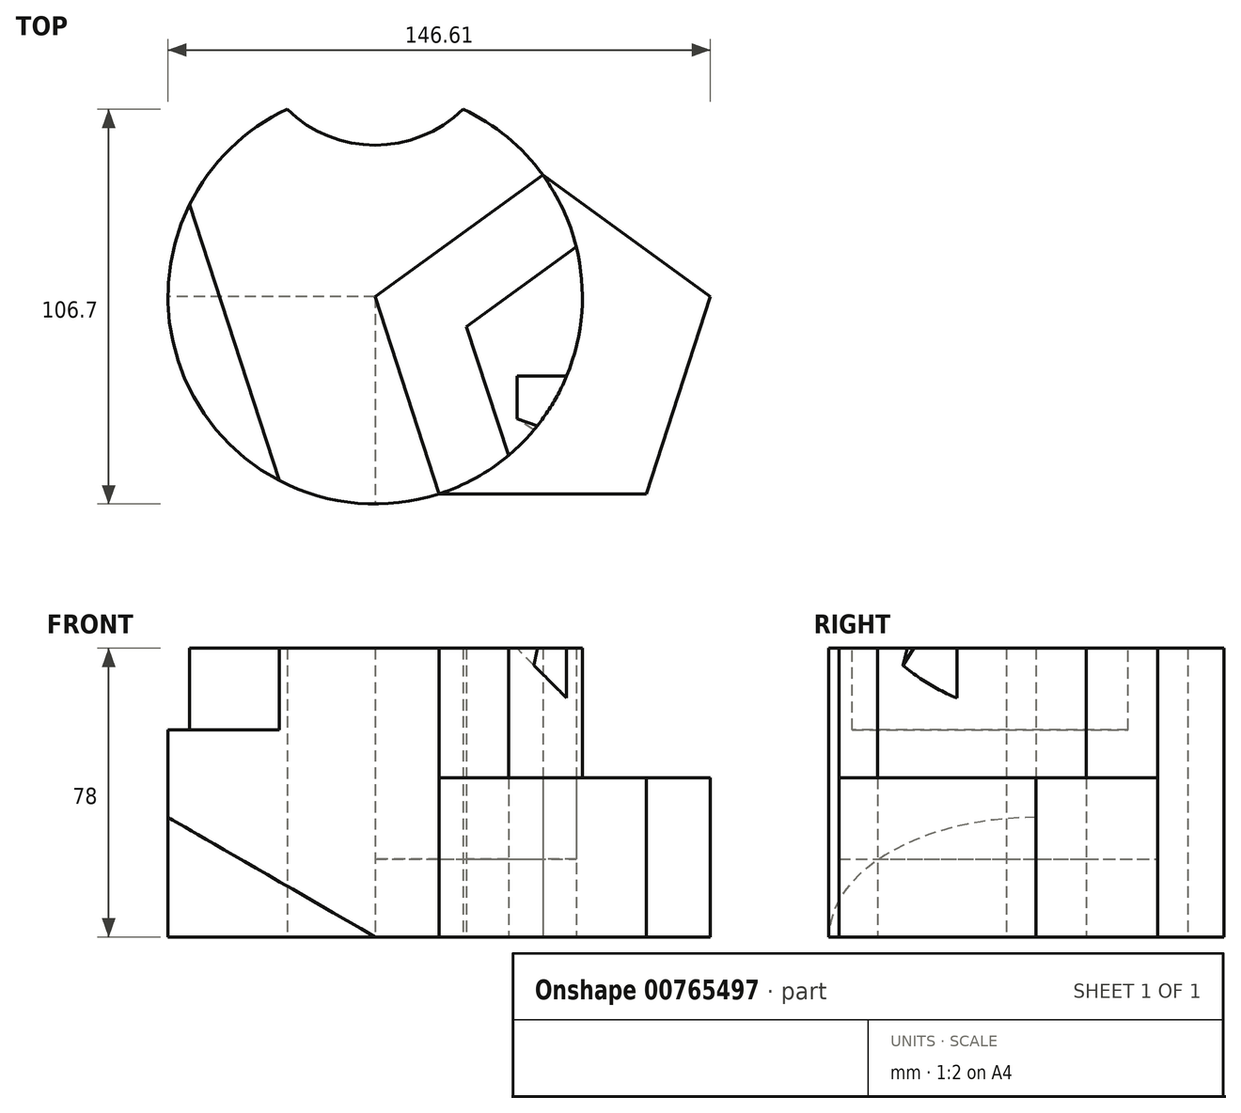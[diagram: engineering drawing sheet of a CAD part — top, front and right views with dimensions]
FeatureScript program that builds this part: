
annotation { "Feature Type Name" : "Feature", "Feature Type Description" : "" }
export const myFeature = defineFeature(function(context is Context, id is Id, definition is map)
    precondition{}
    {
        {
            var Q0;
            Q0=qCreatedBy(makeId("Top.planeOp"),FACE);
            var sketch = newSketch(context, id + "F0", { "sketchPlane" : qUnion([Q0])});
            skCircle(sketch, "E0.cCircle", {"center": v(45.3, -14.72) * mm, "radius": 47.64 * mm, "construction": true});
            skLineSegment(sketch, "E0.0", {"start": v(0, 0) * mm, "end": v(45.3, 32.92) * mm});
            skLineSegment(sketch, "E0.1", {"start": v(45.3, 32.92) * mm, "end": v(90.6, 0) * mm});
            skLineSegment(sketch, "E0.2", {"start": v(90.6, 0) * mm, "end": v(73.3, -53.26) * mm});
            skLineSegment(sketch, "E0.3", {"start": v(73.3, -53.26) * mm, "end": v(17.3, -53.26) * mm});
            skLineSegment(sketch, "E0.4", {"start": v(17.3, -53.26) * mm, "end": v(0, 0) * mm});
            skLineSegment(sketch, "E1", {"start": v(0, 0) * mm, "end": v(56, 0) * mm, "construction": true});
            skLineSegment(sketch, "E2", {"start": v(0, 0) * mm, "end": v(0, 75) * mm, "construction": true});
            skArc(sketch, "E3", {"start": v(-23.78, 50.7) * mm, "mid": v(0, -56) * mm, "end": v(23.78, 50.7) * mm});
            skArc(sketch, "E4", {"start": v(-23.78, 50.7) * mm, "mid": v(0, 41) * mm, "end": v(23.78, 50.7) * mm});
            skLineSegment(sketch, "E5", {"start": v(45.3, -14.72) * mm, "end": v(0, 0) * mm, "construction": true});
            skLineSegment(sketch, "E6", {"start": v(36.01, -42.88) * mm, "end": v(24.69, -8.02) * mm});
            skLineSegment(sketch, "E7", {"start": v(24.69, -8.02) * mm, "end": v(54.34, 13.52) * mm});
            skSolve(sketch);
        }
        {
            var Q0;
            {var subQ1=sQuery(id+"F0.wireOp",EDGE,"E0.0");Q0=makeQuery(id+"F0.imprint","IMPRINT",FACE,{"disambiguationData":[TD([[makeQuery(id+"F0.imprint","IMPRINT",EDGE,{"derivedFrom":subQ1}),1.0]])]});}
            var Q1;
            {var subQ0=sQuery(id+"F0.wireOp",EDGE,"E6");Q1=makeQuery(id+"F0.imprint","IMPRINT",FACE,{"disambiguationData":[TD([[makeQuery(id+"F0.imprint","IMPRINT",EDGE,{"derivedFrom":subQ0}),-1.0]])]});}
            extrude(context, id + "F1", {"entities" : qUnion([Q0, Q1]), "depth" : 78 * mm, "offsetDistance" : 25 * mm});
        }
        {
            var Q0;
            {var subQ3=sQuery(id+"F0.wireOp",EDGE,"E0.1");Q0=makeQuery(id+"F0.imprint","IMPRINT",FACE,{"disambiguationData":[TD([[makeQuery(id+"F0.imprint","IMPRINT",EDGE,{"derivedFrom":subQ3}),-1.0]])]});}
            extrude(context, id + "F2", {"entities" : qUnion([Q0]), "operationType" : NewBodyOperationType.ADD, "depth" : 43 * mm, "offsetDistance" : 25 * mm});
        }
        {
            var Q0;
            Q0=makeQuery(id+"F1.opExtrude","CAP_FACE",FACE,{"disambiguationData":[OSD([sQuery(id+"F0.wireOp",EDGE,"E3"),sQuery(id+"F0.wireOp",EDGE,"E4")])],"isStart":false});
            var sketch = newSketch(context, id + "F3", { "sketchPlane" : qUnion([Q0])});
            skLineSegment(sketch, "E8", {"start": v(-25.93, -49.63) * mm, "end": v(-50.15, 24.91) * mm});
            skSolve(sketch);
        }
        {
            var Q0;
            {var subQ0=sQuery(id+"F3.wireOp",EDGE,"E8");Q0=makeQuery(id+"F3.imprint","IMPRINT",FACE,{"disambiguationData":[TD([[makeQuery(id+"F3.imprint","IMPRINT",EDGE,{"derivedFrom":subQ0}),1.0]])]});}
            extrude(context, id + "F4", {"entities" : qUnion([Q0]), "operationType" : NewBodyOperationType.REMOVE, "oppositeDirection" : true, "depth" : 22 * mm, "offsetDistance" : 25 * mm});
        }
        {
            var Q0;
            Q0=qCreatedBy(makeId("Front.planeOp"),FACE);
            cPlane(context, id + "F5", {"entities" : qUnion([Q0]), "cplaneType" : CPlaneType.OFFSET, "offset" : 56 * mm, "width" : 150 * mm, "height" : 150 * mm});
        }
        {
            var Q0;
            Q0=qCreatedBy(id+"F5.planeOp",FACE);
            var sketch = newSketch(context, id + "F6", { "sketchPlane" : qUnion([Q0])});
            skLineSegment(sketch, "E9", {"start": v(0, 0) * mm, "end": v(-56, 0) * mm});
            skLineSegment(sketch, "E10", {"start": v(0, 0) * mm, "end": v(-56, 32.33) * mm});
            skLineSegment(sketch, "E11", {"start": v(-56, 32.33) * mm, "end": v(-56, 0) * mm});
            skSolve(sketch);
        }
        {
            var Q0;
            Q0=makeQuery(id+"F6.imprint","IMPRINT",FACE,{"disambiguationData":[TD([[makeQuery(id+"F6.imprint","IMPRINT",EDGE,{"derivedFrom":sQuery(id+"F6.wireOp",EDGE,"E9")}),-1.0]])]});
            extrude(context, id + "F7", {"entities" : qUnion([Q0]), "operationType" : NewBodyOperationType.REMOVE, "oppositeDirection" : true, "depth" : 56 * mm, "offsetDistance" : 25 * mm});
        }
        {
            var Q0;
            Q0=makeQuery(id+"F2.opExtrude","CAP_FACE",FACE,{"disambiguationData":[OSD([sQuery(id+"F0.wireOp",EDGE,"E0.1"),sQuery(id+"F0.wireOp",EDGE,"E0.2"),sQuery(id+"F0.wireOp",EDGE,"E0.3"),sQuery(id+"F0.wireOp",EDGE,"E3")])],"isStart":false});
            var sketch = newSketch(context, id + "F8", { "sketchPlane" : qUnion([Q0])});
            skLineSegment(sketch, "E12", {"start": v(73.3, -53.26) * mm, "end": v(73.3, 12.57) * mm});
            skSolve(sketch);
        }
        {
            var Q0;
            {var subQ0=sQuery(id+"F8.wireOp",EDGE,"E12");Q0=makeQuery(id+"F8.imprint","IMPRINT",FACE,{"disambiguationData":[TD([[makeQuery(id+"F8.imprint","IMPRINT",EDGE,{"derivedFrom":subQ0}),-1.0]])]});}
            var Q1;
            Q1=sQuery(id+"F8.wireOp",EDGE,"E12");
            cPlane(context, id + "F9", {"entities" : qUnion([Q0, Q1]), "cplaneType" : CPlaneType.LINE_ANGLE, "offset" : 25 * mm, "angle" : 45 * degree, "width" : 150 * mm, "height" : 150 * mm});
        }
        {
            var Q0;
            Q0=qCreatedBy(id+"F9.planeOp",FACE);
            var sketch = newSketch(context, id + "F10", { "sketchPlane" : qUnion([Q0])});
            skLineSegment(sketch, "E13", {"start": v(45.9, 0) * mm, "end": v(21.43, 53.26) * mm});
            skLineSegment(sketch, "E14", {"start": v(21.43, -12.57) * mm, "end": v(45.9, 0) * mm});
            skLineSegment(sketch, "E15", {"start": v(21.43, -12.57) * mm, "end": v(21.43, 53.26) * mm});
            skSolve(sketch);
        }
        {
            var Q0;
            Q0=makeQuery(id+"F10.imprint","IMPRINT",FACE,{"disambiguationData":[TD([[makeQuery(id+"F10.imprint","IMPRINT",EDGE,{"derivedFrom":sQuery(id+"F10.wireOp",EDGE,"E13")}),1.0]])]});
            var Q1;
            Q1=sQuery(id+"F10.wireOp",EDGE,"E13");
            var Q2;
            Q2=sQuery(id+"F10.wireOp",EDGE,"E14");
            var Q3;
            Q3=sQuery(id+"F8.wireOp",EDGE,"E12");
            extrude(context, id + "F11", {"entities" : qUnion([Q0]), "operationType" : NewBodyOperationType.REMOVE, "surfaceEntities" : qUnion([Q1, Q2, Q3]), "oppositeDirection" : true, "depth" : 15 * mm, "offsetDistance" : 25 * mm});
        }
        {
            var Q0;
            {var subQ1=sQuery(id+"F0.wireOp",EDGE,"E0.0");Q0=makeQuery(id+"F0.imprint","IMPRINT",FACE,{"disambiguationData":[TD([[makeQuery(id+"F0.imprint","IMPRINT",EDGE,{"derivedFrom":subQ1}),-1.0]])]});}
            extrude(context, id + "F12", {"entities" : qUnion([Q0]), "depth" : 78 * mm, "offsetDistance" : 25 * mm});
        }
        {
            var Q0;
            {var subQ1=sQuery(id+"F0.wireOp",EDGE,"E0.0");Q0=makeQuery(id+"F0.imprint","IMPRINT",FACE,{"disambiguationData":[TD([[makeQuery(id+"F0.imprint","IMPRINT",EDGE,{"derivedFrom":subQ1}),-1.0]])]});}
            extrude(context, id + "F13", {"entities" : qUnion([Q0]), "operationType" : NewBodyOperationType.REMOVE, "depth" : 21 * mm, "offsetDistance" : 25 * mm});
        }
        {
            var Q0;
            Q0=makeQuery(id+"F10.imprint","IMPRINT",FACE,{"disambiguationData":[TD([[makeQuery(id+"F10.imprint","IMPRINT",EDGE,{"derivedFrom":sQuery(id+"F10.wireOp",EDGE,"E13")}),1.0]])]});
            var Q1;
            Q1=sQuery(id+"F10.wireOp",EDGE,"E13");
            var Q2;
            Q2=sQuery(id+"F10.wireOp",EDGE,"E15");
            var Q3;
            Q3=sQuery(id+"F10.wireOp",EDGE,"E14");
            extrude(context, id + "F14", {"entities" : qUnion([Q0]), "operationType" : NewBodyOperationType.REMOVE, "surfaceEntities" : qUnion([Q1, Q2, Q3]), "oppositeDirection" : true, "depth" : 15 * mm, "offsetDistance" : 25 * mm});
        }
    });
